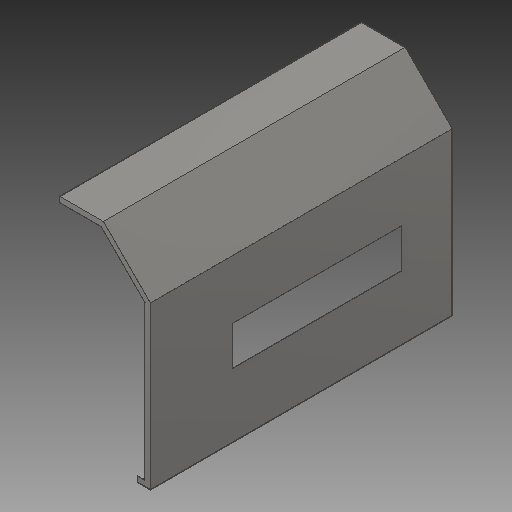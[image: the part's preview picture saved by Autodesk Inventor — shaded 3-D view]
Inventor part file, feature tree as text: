
AUTODESK INVENTOR PART (.ipt)
format: ipt  version: 2018 (Build 220112000, 112)  size: 180,224 bytes
history: native  units: mm
features: extrude x6, sketch x6, projected_geometry x1
ambient origin geometry x8: Origin, YZ Plane, XZ Plane, XY Plane, X Axis, Y Axis, Z Axis, Center Point
bodies: Solid1 (feature_tree)
feature tree (13):
  extrude  "Extrusion1"  TaperAngle=45.0deg  [1 undecoded]
  extrude  "Extrusion3"  Depth=50.0mm
  extrude  "Extrusion4"  Depth=195.0mm
  extrude  "Extrusion5"  Depth=650.0mm
  extrude  "Extrusion6"  Depth=150.0mm
  extrude  "Extrusion7"  Depth=1.6mm
  sketch  "Sketch1"  dims[d0=167.6mm d1=45.0deg]
  sketch  "Sketch2"  dims[d2=800.0mm d4=50.0mm]
  sketch  "Sketch3"  dims[d6=1160.0mm d7=0.0mm d8=195.0mm]
  sketch  "Sketch4"  dims[d10=650.0mm d11=650.0mm]
  projected_geometry  "Projected Loop1"
  sketch  "Sketch5"  dims[d12=150.0mm d15=180.0mm]
  sketch  "Sketch6"  dims[d19=1.6mm d20=320.0mm d21=10.0mm d22=0.0mm d23=20.0mm d24=1.6mm d25=0.0mm d26=1.6mm d27=0.0mm d28=1.6mm d29=0.0mm d30=1.6mm d31=1.6mm d32=1.6mm d33=0.0mm]
note: 1 required parameter value undecoded (feature->parameter linkage not recoverable at this tier; creation-order binding heuristic only, values carry confidence <= 0.55)
